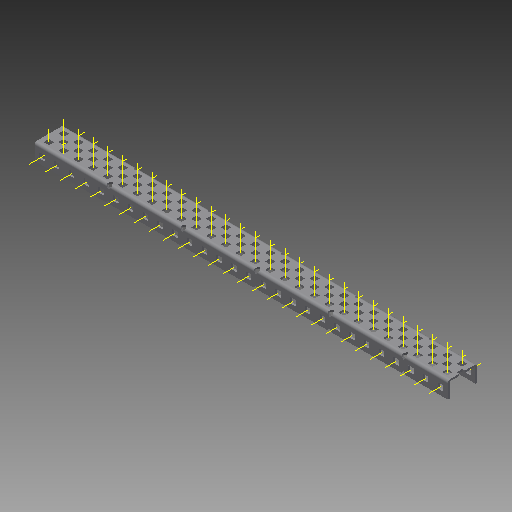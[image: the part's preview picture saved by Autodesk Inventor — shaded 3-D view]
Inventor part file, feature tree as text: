
AUTODESK INVENTOR PART (.ipt)
format: ipt  version: 2017 (Build 210142000, 142)  size: 2,156,544 bytes
history: native  units: in
note: dims shown in document units (in); Inventor stores cm internally (conversion verified against a paired STEP export)
features: other x146, pattern_linear x3, sheet_metal_op x1, extrude x1, imported_body x1, sketch x1
ambient origin geometry x8: Origin, YZ Plane, XZ Plane, XY Plane, X Axis, Y Axis, Z Axis, Center Point
bodies: Body1 (feature_tree)
feature tree (153):
  sheet_metal_op  "Fold1"
  other  "C-Channel"
  extrude  "length cut"  Depth=0.5in
  other  "top axis"
  other  "inner axis"
  other  "front axis"
  other  "back axis"
  pattern_linear  "top axes"  Spacing1=0.5in  [1 undecoded]
  pattern_linear  "inner axes"  Spacing1=0.5in  [1 undecoded]
  pattern_linear  "horiz axes"  Spacing1=-14.0in  [1 undecoded]
  other  "right plane"
  imported_body  "Base1"
  sketch  "Sketch1"  dims[d1=0.0in d4=0.5in d5=0.7874in d7=0.5in d10=0.5in d13=0.5in d14=-14.0in d15=0.0in d16=0.0in d17=0.0in d18=0.0in d19=0.0in]
  other  "Work Point1"
  other  "Work Point2"
  other  "Work Point3"
  other  "Work Point4"
  other  "Work Axis5"
  other  "Work Axis6"
  other  "Work Axis7"
  other  "Work Axis8"
  other  "Work Axis11"
  other  "Work Axis12"
  other  "Work Axis13"
  other  "Work Axis14"
  other  "Work Axis15"
  other  "Work Axis18"
  other  "Work Axis19"
  other  "Work Axis20"
  other  "Work Axis23"
  other  "Work Axis24"
  other  "Work Axis25"
  other  "Work Axis26"
  other  "Work Axis30"
  other  "Work Axis31"
  other  "Work Axis32"
  other  "Work Axis33"
  other  "left plane"
  other  "Work Axis37"
  other  "Work Axis38"
  other  "Work Axis39"
  other  "Work Axis40"
  other  "Work Axis41"
  other  "Work Axis42"
  other  "Work Axis43"
  other  "Work Axis44"
  other  "Work Axis45"
  other  "Work Axis46"
  other  "Work Axis47"
  other  "Work Axis48"
  other  "Work Axis49"
  other  "Work Axis50"
  other  "Work Axis51"
  other  "Work Axis52"
  other  "Work Axis53"
  other  "Work Axis54"
  other  "Work Axis55"
  other  "Work Axis56"
  other  "Work Axis57"
  other  "Work Axis58"
  other  "Work Axis59"
  other  "Work Axis60"
  other  "Work Axis61"
  other  "Work Axis62"
  other  "Work Axis63"
  other  "Work Axis64"
  other  "Work Axis65"
  other  "Work Axis66"
  other  "Work Axis67"
  other  "Work Axis68"
  other  "Work Axis69"
  other  "Work Axis70"
  other  "Work Axis71"
  other  "Work Axis72"
  other  "Work Axis73"
  other  "Work Axis74"
  other  "Work Axis75"
  other  "Work Axis76"
  other  "Work Axis77"
  other  "Work Axis78"
  other  "Work Axis79"
  other  "Work Axis80"
  other  "Work Axis81"
  other  "Work Axis82"
  other  "Work Axis83"
  other  "Work Axis84"
  other  "Work Axis85"
  other  "Work Axis86"
  other  "Work Axis87"
  other  "Work Axis88"
  other  "Work Axis89"
  other  "Work Axis90"
  other  "Work Axis91"
  other  "Work Axis92"
  other  "Work Axis93"
  other  "Work Axis94"
  other  "Work Axis95"
  other  "Work Axis96"
  other  "Work Axis97"
  other  "Work Axis98"
  other  "Work Axis99"
  other  "Work Axis100"
  other  "Work Axis101"
  other  "Work Axis102"
  other  "Work Axis103"
  other  "Work Axis104"
  other  "Work Axis105"
  other  "Work Axis106"
  other  "Work Axis107"
  other  "Work Axis108"
  other  "Work Axis109"
  other  "Work Axis110"
  other  "Work Axis111"
  other  "Work Axis112"
  other  "Work Axis113"
  other  "Work Axis114"
  other  "Work Axis115"
  other  "Work Axis116"
  other  "Work Axis117"
  other  "Work Axis118"
  other  "Work Axis119"
  other  "Work Axis120"
  other  "Work Axis121"
  other  "Work Axis122"
  other  "Work Axis123"
  other  "Work Axis124"
  other  "Work Axis125"
  other  "Work Axis126"
  other  "Work Axis127"
  other  "Work Axis128"
  other  "Work Axis129"
  other  "Work Axis130"
  other  "Work Axis131"
  other  "Work Axis132"
  other  "Work Axis133"
  other  "Work Axis134"
  other  "Work Axis135"
  other  "Work Axis136"
  other  "Work Axis137"
  other  "Work Axis138"
  other  "Work Axis140"
  other  "Work Axis141"
  other  "Work Axis143"
  other  "Work Axis144"
  other  "Work Axis146"
  other  "Work Axis147"
  other  "Work Axis149"
  other  "Work Axis150"
  other  "Work Axis152"
  other  "Work Axis153"
  other  "Work Axis154"
  other  "Work Axis155"
  other  "Work Axis156"
note: 3 required parameter values undecoded (feature->parameter linkage not recoverable at this tier; creation-order binding heuristic only, values carry confidence <= 0.55)
